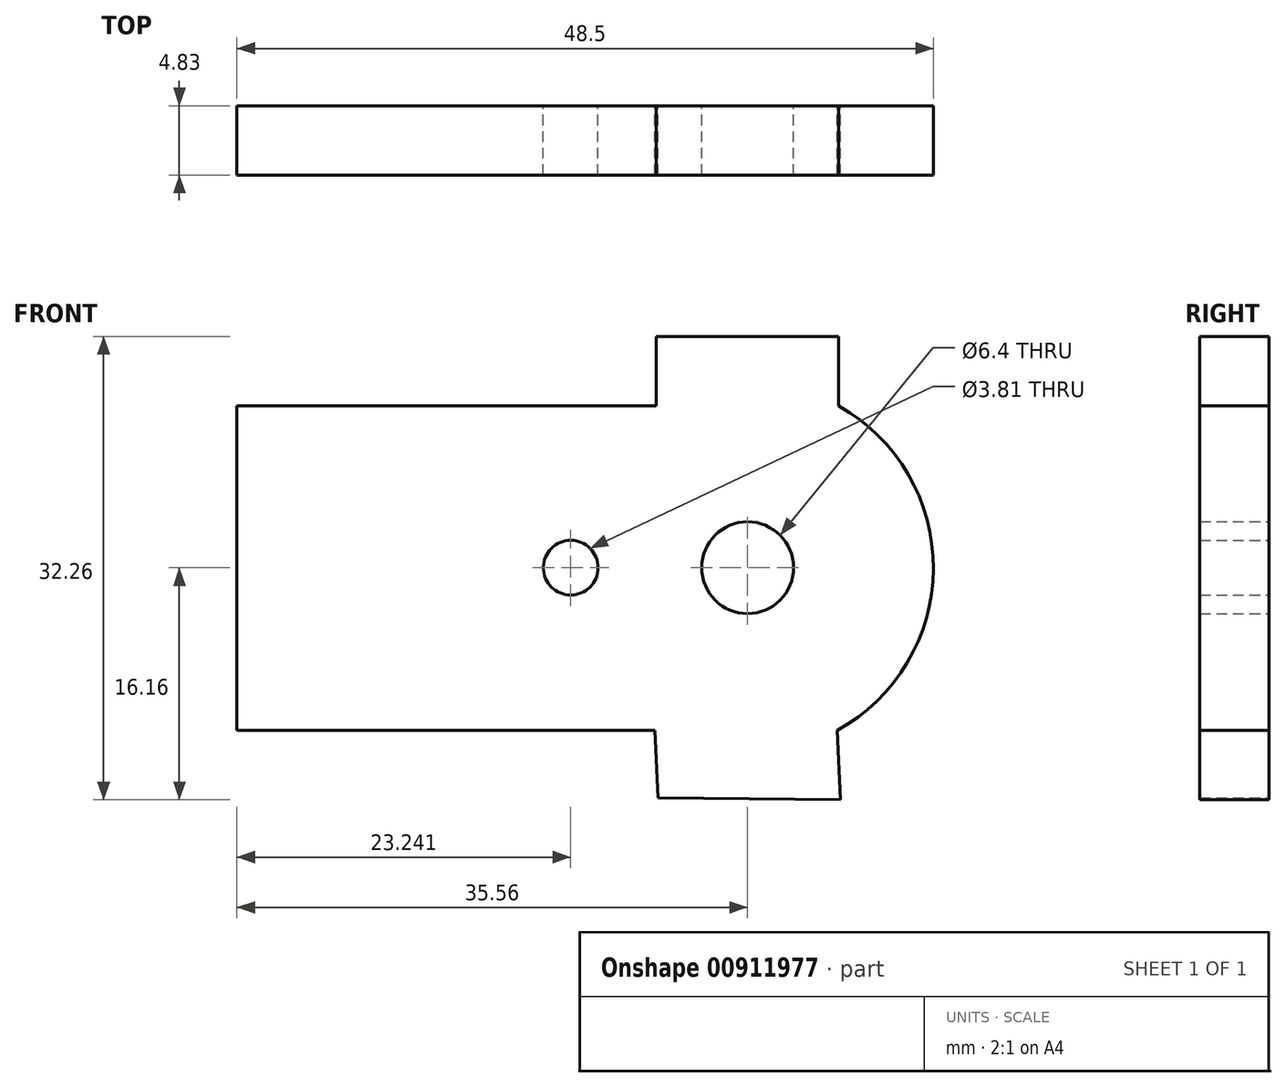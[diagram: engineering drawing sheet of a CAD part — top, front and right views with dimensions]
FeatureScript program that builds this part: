
annotation { "Feature Type Name" : "Feature", "Feature Type Description" : "" }
export const myFeature = defineFeature(function(context is Context, id is Id, definition is map)
    precondition{}
    {
        {
            var Q0;
            Q0=qCreatedBy(makeId("Front.planeOp"),FACE);
            var sketch = newSketch(context, id + "F0", { "sketchPlane" : qUnion([Q0])});
            skLineSegment(sketch, "E0.bottom", {"start": v(6.47, -16.16) * mm, "end": v(-6.23, -16.02) * mm});
            skLineSegment(sketch, "E0.left", {"start": v(6.47, -16.16) * mm, "end": v(6.23, -11.34) * mm});
            skLineSegment(sketch, "E0.right", {"start": v(-6.23, -16.02) * mm, "end": v(-6.47, -11.2) * mm});
            skPoint(sketch, "E0.middle", {"position": v(0, -13.68) * mm});
            skArc(sketch, "E1", {"start": v(6.23, -11.34) * mm, "mid": v(12.94, -0.07) * mm, "end": v(6.35, 11.27) * mm});
            skPoint(sketch, "E2.center", {"position": v(0, -0.04) * mm});
            skLineSegment(sketch, "E3.top", {"start": v(6.35, 16.1) * mm, "end": v(-6.35, 16.1) * mm});
            skLineSegment(sketch, "E3.left", {"start": v(6.35, 11.27) * mm, "end": v(6.35, 16.1) * mm});
            skLineSegment(sketch, "E3.right", {"start": v(-6.35, 11.27) * mm, "end": v(-6.35, 16.1) * mm});
            skPoint(sketch, "E3.middle", {"position": v(0, 13.68) * mm});
            skCircle(sketch, "E4", {"center": v(0, 0) * mm, "radius": 3.2 * mm});
            skLineSegment(sketch, "E5.bottom", {"start": v(-6.35, 11.27) * mm, "end": v(-35.56, 11.27) * mm});
            skLineSegment(sketch, "E5.top", {"start": v(6.35, -11.34) * mm, "end": v(6.23, -11.34) * mm});
            skLineSegment(sketch, "E5.right", {"start": v(-35.56, 11.27) * mm, "end": v(-35.56, -11.34) * mm});
            skLineSegment(sketch, "E6.trimOffspring", {"start": v(-6.46, -11.34) * mm, "end": v(-35.56, -11.34) * mm});
            skCircle(sketch, "E7.MirrorC", {"center": v(-12.32, 0) * mm, "radius": 1.9 * mm});
            skSolve(sketch);
        }
        {
            var Q0;
            {var subQ1=sQuery(id+"F0.wireOp",EDGE,"4319f0a5-6fa3-4e93-b0d5-62a2f58796ac.trimOffspring");Q0=makeQuery(id+"F0.imprint","IMPRINT",FACE,{"disambiguationData":[TD([[makeQuery(id+"F0.imprint","IMPRINT",EDGE,{"derivedFrom":subQ1}),-1.0]])]});}
            var Q1;
            Q1=makeQuery(id+"F0.imprint","IMPRINT",FACE,{"disambiguationData":[TD([[makeQuery(id+"F0.imprint","IMPRINT",EDGE,{"derivedFrom":sQuery(id+"F0.wireOp",EDGE,"E4")}),-1.0]])]});
            var Q2;
            Q2=makeQuery(id+"F0.imprint","IMPRINT",FACE,{"disambiguationData":[TD([[makeQuery(id+"F0.imprint","IMPRINT",EDGE,{"derivedFrom":sQuery(id+"F0.wireOp",EDGE,"E3.top")}),1.0]])]});
            var Q3;
            {var subQ0=sQuery(id+"F0.wireOp",EDGE,"E0.bottom");Q3=makeQuery(id+"F0.imprint","IMPRINT",FACE,{"disambiguationData":[TD([[makeQuery(id+"F0.imprint","IMPRINT",EDGE,{"derivedFrom":subQ0}),-1.0]])]});}
            var Q4;
            {var subQ0=sQuery(id+"F0.wireOp",EDGE,"E5.left");var subQ1=sQuery(id+"F0.wireOp",EDGE,"E1");var subQ3=makeQuery(id+"F0.imprint","INTERSECT",VERTEX,{"derivedFrom":[subQ1,subQ0]});Q4=makeQuery(id+"F0.imprint","IMPRINT",FACE,{"disambiguationData":[TD([[makeQuery(id+"F0.imprint","IMPRINT",EDGE,{"disambiguationData":[TD([[subQ3,-1.0]])],"derivedFrom":subQ1}),1.0]])]});}
            extrude(context, id + "F1", {"entities" : qUnion([Q0, Q1, Q2, Q3, Q4]), "depth" : 4.83 * mm, "offsetDistance" : 25.4 * mm});
        }
    });
